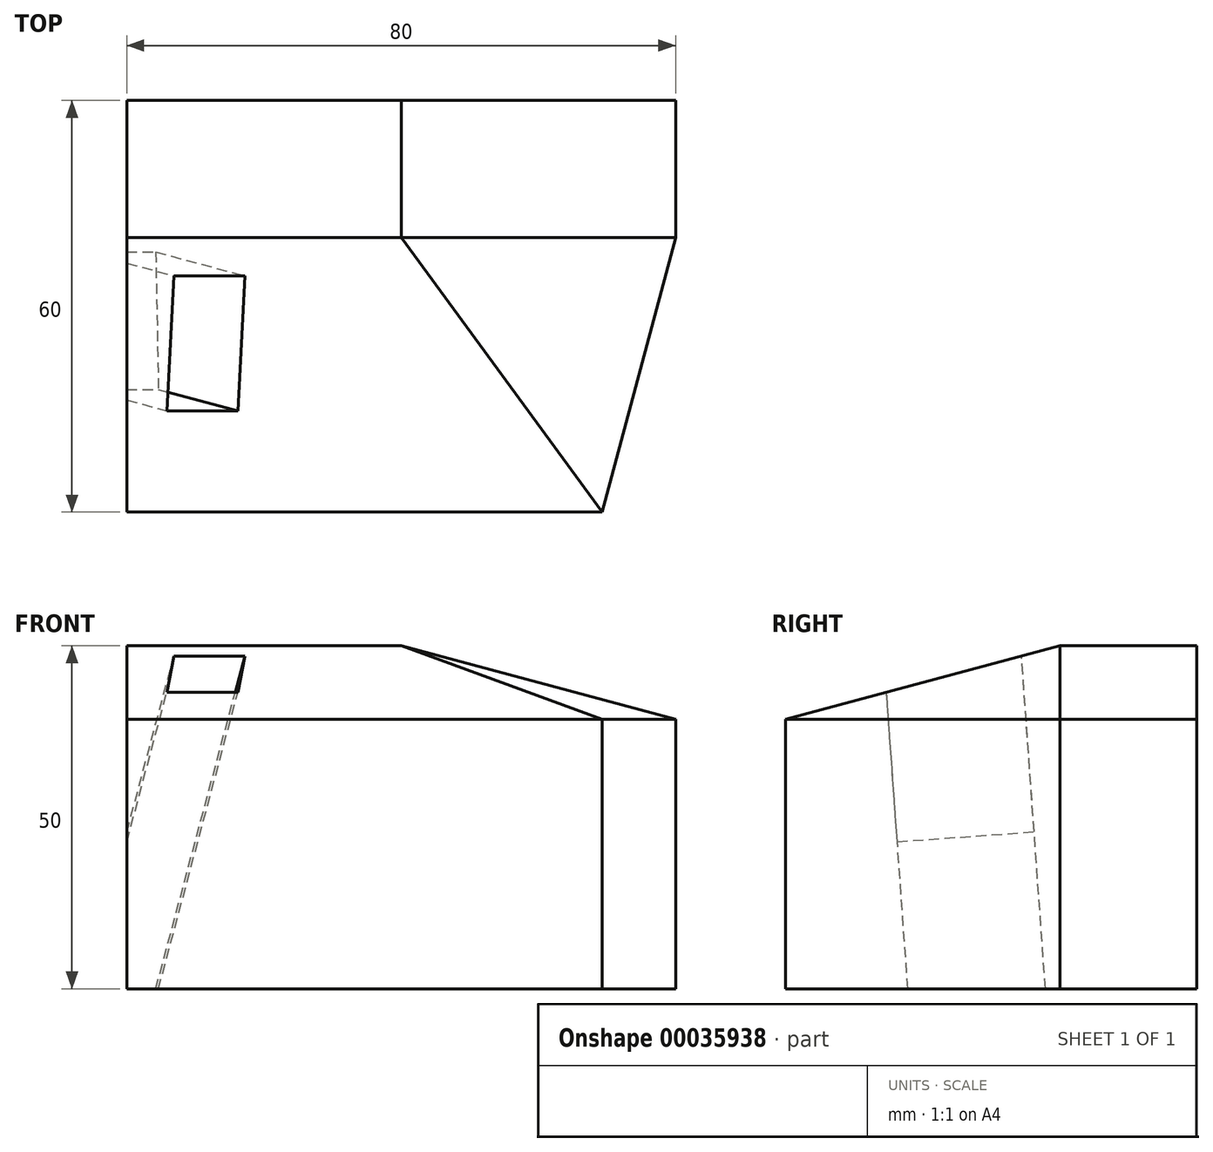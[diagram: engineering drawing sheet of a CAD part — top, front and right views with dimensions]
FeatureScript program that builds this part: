
annotation { "Feature Type Name" : "Feature", "Feature Type Description" : "" }
export const myFeature = defineFeature(function(context is Context, id is Id, definition is map)
    precondition{}
    {
        {
            var Q0;
            Q0=qCreatedBy(makeId("Front.planeOp"),FACE);
            var sketch = newSketch(context, id + "F0", { "sketchPlane" : qUnion([Q0])});
            skLineSegment(sketch, "E0.bottom", {"start": v(0, 0) * mm, "end": v(80, 0) * mm});
            skLineSegment(sketch, "E0.top", {"start": v(0, 50) * mm, "end": v(80, 50) * mm});
            skLineSegment(sketch, "E0.left", {"start": v(0, 0) * mm, "end": v(0, 50) * mm});
            skLineSegment(sketch, "E0.right", {"start": v(80, 0) * mm, "end": v(80, 50) * mm});
            skSolve(sketch);
        }
        {
            var Q0;
            Q0 = qSketchRegion(id + "F0", true);
            extrude(context, id + "F1", {"entities" : qUnion([Q0]), "depth" : 60 * mm});
        }
        {
            var Q0;
            Q0=makeQuery(id+"F1.opExtrude","CAP_EDGE",EDGE,{"disambiguationData":[OSD([sQuery(id+"F0.wireOp",EDGE,"E0.top")])],"isStart":false});
            var Q1;
            Q1=makeQuery(id+"F1.opExtrude","SWEPT_EDGE",EDGE,{"disambiguationData":[OSD([sQuery(id+"F0.wireOp",EDGE,"E0.top"),sQuery(id+"F0.wireOp",EDGE,"E0.right")])]});
            var Q2;
            Q2=makeQuery(id+"F1.opExtrude","CAP_EDGE",EDGE,{"disambiguationData":[OSD([sQuery(id+"F0.wireOp",EDGE,"E0.right")])],"isStart":false});
            chamfer(context, id + "F2", {"entities" : qUnion([Q0, Q1, Q2]), "chamferType" : ChamferType.OFFSET_ANGLE, "width" : 40 * mm, "oppositeDirection" : false, "angle" : 15 * degree, "tangentPropagation" : true});
        }
        {
            var Q0;
            {var subQ0=sQuery(id+"F0.wireOp",EDGE,"E0.top");var subQ1=sQuery(id+"F0.wireOp",EDGE,"E0.right");Q0=makeQuery(id+"F2.opChamfer","BLEND_FACE",FACE,{"disambiguationData":[OSD([subQ0,subQ1]),TDD([makeQuery(id+"F1.opExtrude","CAP_VERTEX",VERTEX,{"disambiguationData":[OSD([subQ0,subQ1])],"isStart":false})])]});}
            var sketch = newSketch(context, id + "F3", { "sketchPlane" : qUnion([Q0])});
            skLineSegment(sketch, "E1.bottom", {"start": v(-6.33, -22.03) * mm, "end": v(3.67, -22.03) * mm});
            skLineSegment(sketch, "E1.top", {"start": v(-6.33, -42.03) * mm, "end": v(3.67, -42.03) * mm});
            skLineSegment(sketch, "E1.left", {"start": v(-6.33, -22.03) * mm, "end": v(-6.33, -42.03) * mm});
            skLineSegment(sketch, "E1.right", {"start": v(3.67, -22.03) * mm, "end": v(3.67, -42.03) * mm});
            skSolve(sketch);
        }
        {
            var Q0;
            Q0 = qSketchRegion(id + "F3", true);
            extrude(context, id + "F4", {"entities" : qUnion([Q0]), "operationType" : NewBodyOperationType.REMOVE, "endBound" : BoundingType.THROUGH_ALL, "oppositeDirection" : true, "depth" : 25 * mm});
        }
    });
